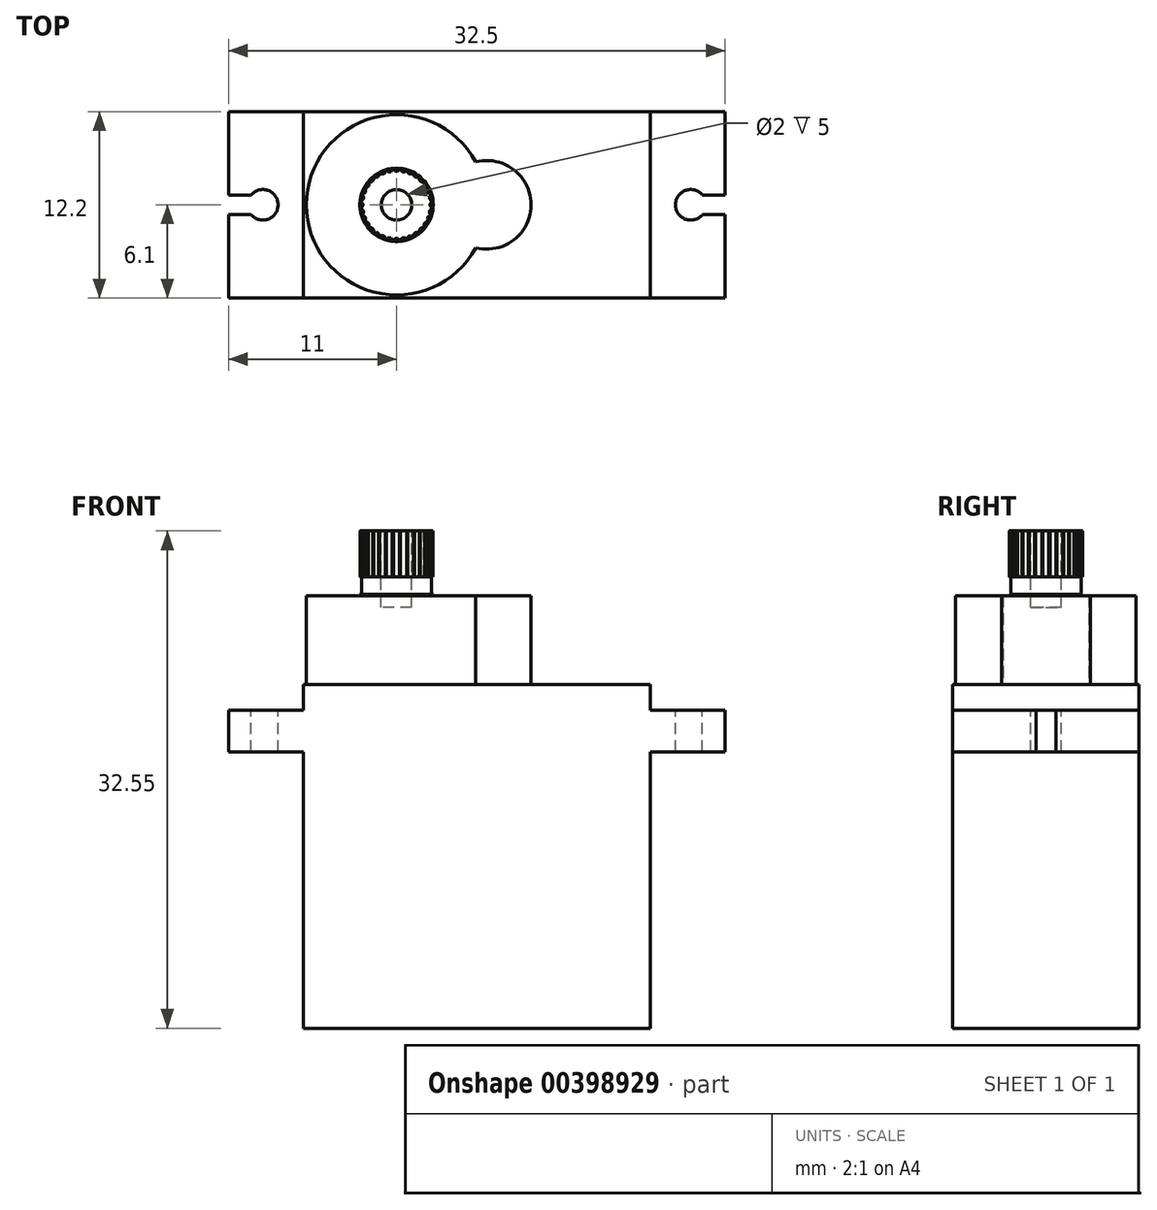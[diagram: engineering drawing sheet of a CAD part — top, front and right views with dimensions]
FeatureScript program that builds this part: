
annotation { "Feature Type Name" : "Feature", "Feature Type Description" : "" }
export const myFeature = defineFeature(function(context is Context, id is Id, definition is map)
    precondition{}
    {
        {
            var Q0;
            Q0=qCreatedBy(makeId("Front.planeOp"),FACE);
            var sketch = newSketch(context, id + "F0", { "sketchPlane" : qUnion([Q0])});
            skLineSegment(sketch, "E0.bottom", {"start": v(11.35, 0) * mm, "end": v(-11.35, 0) * mm});
            skLineSegment(sketch, "E0.top", {"start": v(11.35, 22.5) * mm, "end": v(-11.35, 22.5) * mm});
            skLineSegment(sketch, "E0.left", {"start": v(11.35, 0) * mm, "end": v(11.35, 18.1) * mm});
            skLineSegment(sketch, "E0.right", {"start": v(-11.35, 0) * mm, "end": v(-11.35, 18.1) * mm});
            skLineSegment(sketch, "E1.bottom", {"start": v(11.35, 20.8) * mm, "end": v(16.25, 20.8) * mm});
            skLineSegment(sketch, "E1.top", {"start": v(11.35, 18.1) * mm, "end": v(16.25, 18.1) * mm});
            skLineSegment(sketch, "E1.right", {"start": v(16.25, 20.8) * mm, "end": v(16.25, 18.1) * mm});
            skLineSegment(sketch, "E2.bottom", {"start": v(-11.35, 20.8) * mm, "end": v(-16.25, 20.8) * mm});
            skLineSegment(sketch, "E2.top", {"start": v(-11.35, 18.1) * mm, "end": v(-16.25, 18.1) * mm});
            skLineSegment(sketch, "E2.right", {"start": v(-16.25, 20.8) * mm, "end": v(-16.25, 18.1) * mm});
            skLineSegment(sketch, "E3.trimOffspring", {"start": v(11.35, 20.8) * mm, "end": v(11.35, 22.5) * mm});
            skLineSegment(sketch, "E4.trimOffspring", {"start": v(-11.35, 20.8) * mm, "end": v(-11.35, 22.5) * mm});
            skSolve(sketch);
        }
        {
            var Q0;
            Q0=makeQuery(id+"F0.imprint","IMPRINT",FACE,{"disambiguationData":[TD([[makeQuery(id+"F0.imprint","IMPRINT",EDGE,{"derivedFrom":sQuery(id+"F0.wireOp",EDGE,"E0.bottom")}),-1.0]])]});
            extrude(context, id + "F1", {"entities" : qUnion([Q0]), "depth" : 12.2 * mm});
        }
        {
            var Q0;
            Q0=makeQuery(id+"F1.opExtrude","SWEPT_FACE",FACE,{"disambiguationData":[OSD([sQuery(id+"F0.wireOp",EDGE,"E0.top")])]});
            var sketch = newSketch(context, id + "F2", { "sketchPlane" : qUnion([Q0])});
            skPoint(sketch, "E5.0", {"position": v(-11.35, -6.1) * mm});
            skArc(sketch, "E6", {"start": v(-0.06, -3.29) * mm, "mid": v(-11.15, -6.1) * mm, "end": v(-0.06, -8.91) * mm});
            skArc(sketch, "E7", {"start": v(-0.06, -8.91) * mm, "mid": v(3.55, -6.1) * mm, "end": v(-0.06, -3.29) * mm});
            skSolve(sketch);
        }
        {
            var Q0;
            Q0 = qSketchRegion(id + "F2", true);
            extrude(context, id + "F3", {"entities" : qUnion([Q0]), "operationType" : NewBodyOperationType.ADD, "depth" : 5.8 * mm});
        }
        {
            var Q0;
            Q0=makeQuery(id+"F3.opExtrude","CAP_FACE",FACE,{"disambiguationData":[OSD([sQuery(id+"F2.wireOp",EDGE,"E6"),sQuery(id+"F2.wireOp",EDGE,"E7")])],"isStart":false});
            var sketch = newSketch(context, id + "F4", { "sketchPlane" : qUnion([Q0])});
            skArc(sketch, "E8.0", {"start": v(-0.06, -3.29) * mm, "mid": v(-11.15, -6.1) * mm, "end": v(-0.06, -8.91) * mm});
            skCircle(sketch, "E9", {"center": v(-5.25, -6.1) * mm, "radius": 2.4 * mm});
            skSolve(sketch);
        }
        {
            var Q0;
            Q0=makeQuery(id+"F4.imprint","IMPRINT",FACE,{"disambiguationData":[TD([[makeQuery(id+"F4.imprint","IMPRINT",EDGE,{"derivedFrom":sQuery(id+"F4.wireOp",EDGE,"E9")}),1.0]])]});
            extrude(context, id + "F5", {"entities" : qUnion([Q0]), "operationType" : NewBodyOperationType.ADD, "depth" : 4.25 * mm});
        }
        {
            var Q0;
            Q0=makeQuery(id+"F1.opExtrude","SWEPT_FACE",FACE,{"disambiguationData":[OSD([sQuery(id+"F0.wireOp",EDGE,"E1.bottom")])]});
            var sketch = newSketch(context, id + "F6", { "sketchPlane" : qUnion([Q0])});
            skArc(sketch, "E10", {"start": v(14.76, -5.45) * mm, "mid": v(13, -6.1) * mm, "end": v(14.76, -6.75) * mm});
            skPoint(sketch, "E10.centerSnap0", {"position": v(16.25, -6.1) * mm});
            skArc(sketch, "E11", {"start": v(-14.76, -6.75) * mm, "mid": v(-13, -6.1) * mm, "end": v(-14.76, -5.45) * mm});
            skLineSegment(sketch, "E12", {"start": v(0, 4.1) * mm, "end": v(0, -15) * mm, "construction": true});
            skLineSegment(sketch, "E13", {"start": v(16.25, -5.45) * mm, "end": v(14.76, -5.45) * mm});
            skLineSegment(sketch, "E14", {"start": v(16.25, -6.75) * mm, "end": v(14.76, -6.75) * mm});
            skLineSegment(sketch, "E15.0", {"start": v(-16.25, -12.2) * mm, "end": v(-16.25, 0) * mm});
            skLineSegment(sketch, "E16", {"start": v(-16.25, -6.75) * mm, "end": v(-14.76, -6.75) * mm});
            skLineSegment(sketch, "E17", {"start": v(-16.25, -5.45) * mm, "end": v(-14.76, -5.45) * mm});
            skLineSegment(sketch, "E18", {"start": v(17.74, -6.1) * mm, "end": v(11.35, -6.1) * mm, "construction": true});
            skLineSegment(sketch, "E19", {"start": v(16.25, -6.75) * mm, "end": v(16.25, -5.45) * mm});
            skSolve(sketch);
        }
        {
            var Q0;
            Q0 = qSketchRegion(id + "F6", true);
            extrude(context, id + "F7", {"entities" : qUnion([Q0]), "operationType" : NewBodyOperationType.REMOVE, "endBound" : BoundingType.THROUGH_ALL, "oppositeDirection" : true, "depth" : 25 * mm});
        }
        {
            var Q0;
            Q0=makeQuery(id+"F5.opExtrude","CAP_FACE",FACE,{"disambiguationData":[OSD([sQuery(id+"F4.wireOp",EDGE,"E9")])],"isStart":false});
            var sketch = newSketch(context, id + "F8", { "sketchPlane" : qUnion([Q0])});
            skCircle(sketch, "E20.0.0", {"center": v(-5.25, -6.1) * mm, "radius": 2.4 * mm, "construction": true});
            skCircle(sketch, "E21", {"center": v(-5.25, -8.5) * mm, "radius": 0.2 * mm});
            skCircle(sketch, "E22.1.0", {"center": v(-4.78, -8.45) * mm, "radius": 0.2 * mm});
            skCircle(sketch, "E22.2.0", {"center": v(-4.33, -8.32) * mm, "radius": 0.2 * mm});
            skCircle(sketch, "E22.3.0", {"center": v(-3.92, -8.1) * mm, "radius": 0.2 * mm});
            skCircle(sketch, "E22.4.0", {"center": v(-3.55, -7.8) * mm, "radius": 0.2 * mm});
            skCircle(sketch, "E22.5.0", {"center": v(-3.25, -7.43) * mm, "radius": 0.2 * mm});
            skCircle(sketch, "E22.6.0", {"center": v(-3.03, -7.02) * mm, "radius": 0.2 * mm});
            skCircle(sketch, "E22.7.0", {"center": v(-2.9, -6.57) * mm, "radius": 0.2 * mm});
            skCircle(sketch, "E22.8.0", {"center": v(-2.85, -6.1) * mm, "radius": 0.2 * mm});
            skCircle(sketch, "E22.9.0", {"center": v(-2.9, -5.63) * mm, "radius": 0.2 * mm});
            skCircle(sketch, "E22.10.0", {"center": v(-3.03, -5.18) * mm, "radius": 0.2 * mm});
            skCircle(sketch, "E22.11.0", {"center": v(-3.25, -4.77) * mm, "radius": 0.2 * mm});
            skCircle(sketch, "E22.12.0", {"center": v(-3.55, -4.4) * mm, "radius": 0.2 * mm});
            skCircle(sketch, "E22.13.0", {"center": v(-3.92, -4.1) * mm, "radius": 0.2 * mm});
            skCircle(sketch, "E22.14.0", {"center": v(-4.33, -3.88) * mm, "radius": 0.2 * mm});
            skCircle(sketch, "E22.15.0", {"center": v(-4.78, -3.75) * mm, "radius": 0.2 * mm});
            skCircle(sketch, "E22.16.0", {"center": v(-5.25, -3.7) * mm, "radius": 0.2 * mm});
            skCircle(sketch, "E22.17.0", {"center": v(-5.72, -3.75) * mm, "radius": 0.2 * mm});
            skCircle(sketch, "E22.18.0", {"center": v(-6.17, -3.88) * mm, "radius": 0.2 * mm});
            skCircle(sketch, "E22.19.0", {"center": v(-6.58, -4.1) * mm, "radius": 0.2 * mm});
            skCircle(sketch, "E22.20.0", {"center": v(-6.95, -4.4) * mm, "radius": 0.2 * mm});
            skCircle(sketch, "E22.21.0", {"center": v(-7.25, -4.77) * mm, "radius": 0.2 * mm});
            skCircle(sketch, "E22.22.0", {"center": v(-7.47, -5.18) * mm, "radius": 0.2 * mm});
            skCircle(sketch, "E22.23.0", {"center": v(-7.6, -5.63) * mm, "radius": 0.2 * mm});
            skCircle(sketch, "E22.24.0", {"center": v(-7.65, -6.1) * mm, "radius": 0.2 * mm});
            skCircle(sketch, "E22.25.0", {"center": v(-7.6, -6.57) * mm, "radius": 0.2 * mm});
            skCircle(sketch, "E22.26.0", {"center": v(-7.47, -7.02) * mm, "radius": 0.2 * mm});
            skCircle(sketch, "E22.27.0", {"center": v(-7.25, -7.43) * mm, "radius": 0.2 * mm});
            skCircle(sketch, "E22.28.0", {"center": v(-6.95, -7.8) * mm, "radius": 0.2 * mm});
            skCircle(sketch, "E22.29.0", {"center": v(-6.58, -8.1) * mm, "radius": 0.2 * mm});
            skCircle(sketch, "E22.30.0", {"center": v(-6.17, -8.32) * mm, "radius": 0.2 * mm});
            skCircle(sketch, "E22.31.0", {"center": v(-5.72, -8.45) * mm, "radius": 0.2 * mm});
            skSolve(sketch);
        }
        {
            var Q0;
            Q0=makeQuery(id+"F1.opExtrude","CAP_FACE",FACE,{"disambiguationData":[OSD([sQuery(id+"F0.wireOp",EDGE,"E0.bottom"),sQuery(id+"F0.wireOp",EDGE,"E0.top"),sQuery(id+"F0.wireOp",EDGE,"E0.left"),sQuery(id+"F0.wireOp",EDGE,"E0.right"),sQuery(id+"F0.wireOp",EDGE,"E1.bottom"),sQuery(id+"F0.wireOp",EDGE,"E1.top"),sQuery(id+"F0.wireOp",EDGE,"E1.right"),sQuery(id+"F0.wireOp",EDGE,"E2.bottom"),sQuery(id+"F0.wireOp",EDGE,"E2.top"),sQuery(id+"F0.wireOp",EDGE,"E2.right"),sQuery(id+"F0.wireOp",EDGE,"E3.trimOffspring"),sQuery(id+"F0.wireOp",EDGE,"E4.trimOffspring")])],"isStart":false});
            var Q1;
            Q1=makeQuery(id+"F1.opExtrude","CAP_FACE",FACE,{"disambiguationData":[OSD([sQuery(id+"F0.wireOp",EDGE,"E0.bottom"),sQuery(id+"F0.wireOp",EDGE,"E0.top"),sQuery(id+"F0.wireOp",EDGE,"E0.left"),sQuery(id+"F0.wireOp",EDGE,"E0.right"),sQuery(id+"F0.wireOp",EDGE,"E1.bottom"),sQuery(id+"F0.wireOp",EDGE,"E1.top"),sQuery(id+"F0.wireOp",EDGE,"E1.right"),sQuery(id+"F0.wireOp",EDGE,"E2.bottom"),sQuery(id+"F0.wireOp",EDGE,"E2.top"),sQuery(id+"F0.wireOp",EDGE,"E2.right"),sQuery(id+"F0.wireOp",EDGE,"E3.trimOffspring"),sQuery(id+"F0.wireOp",EDGE,"E4.trimOffspring")])],"isStart":true});
            cPlane(context, id + "F9", {"entities" : qUnion([Q0, Q1]), "cplaneType" : CPlaneType.MID_PLANE, "offset" : 25 * mm, "width" : 150 * mm, "height" : 150 * mm});
        }
        {
            var Q0;
            Q0=qCreatedBy(id+"F9.planeOp",FACE);
            var sketch = newSketch(context, id + "F10", { "sketchPlane" : qUnion([Q0])});
            skLineSegment(sketch, "E23.bottom", {"start": v(-7.65, 29.55) * mm, "end": v(-7.55, 29.55) * mm});
            skLineSegment(sketch, "E23.top", {"start": v(-7.65, 28.4) * mm, "end": v(-7.55, 28.4) * mm});
            skLineSegment(sketch, "E23.left", {"start": v(-7.65, 29.55) * mm, "end": v(-7.65, 28.4) * mm});
            skLineSegment(sketch, "E23.right", {"start": v(-7.55, 29.55) * mm, "end": v(-7.55, 28.4) * mm});
            skLineSegment(sketch, "E24", {"start": v(-7.65, 28.3) * mm, "end": v(-7.65, 32.55) * mm, "construction": true});
            skSolve(sketch);
        }
        {
            var Q0;
            Q0 = qSketchRegion(id + "F10", true);
            var Q1;
            Q1=makeQuery(id+"F5.opExtrude","SWEPT_FACE",FACE,{"disambiguationData":[OSD([sQuery(id+"F4.wireOp",EDGE,"E9")])]});
            revolve(context, id + "F11", {"operationType" : NewBodyOperationType.REMOVE, "entities" : qUnion([Q0]), "axis" : qUnion([Q1]), "revolveType" : RevolveType.FULL, "oppositeDirection" : true});
        }
        {
            var Q0;
            Q0 = qSketchRegion(id + "F8", true);
            extrude(context, id + "F12", {"entities" : qUnion([Q0]), "operationType" : NewBodyOperationType.REMOVE, "oppositeDirection" : true, "depth" : 3 * mm});
        }
        {
            var Q0;
            Q0=makeQuery(id+"F5.opExtrude","CAP_FACE",FACE,{"disambiguationData":[OSD([sQuery(id+"F4.wireOp",EDGE,"E9")])],"isStart":false});
            var sketch = newSketch(context, id + "F13", { "sketchPlane" : qUnion([Q0])});
            skCircle(sketch, "E25.0", {"center": v(-5.25, -6.1) * mm, "radius": 2.4 * mm, "construction": true});
            skCircle(sketch, "E26", {"center": v(-5.25, -6.1) * mm, "radius": 1 * mm});
            skSolve(sketch);
        }
        {
            var Q0;
            Q0 = qSketchRegion(id + "F13", true);
            extrude(context, id + "F14", {"entities" : qUnion([Q0]), "operationType" : NewBodyOperationType.REMOVE, "oppositeDirection" : true, "depth" : 5 * mm});
        }
    });
